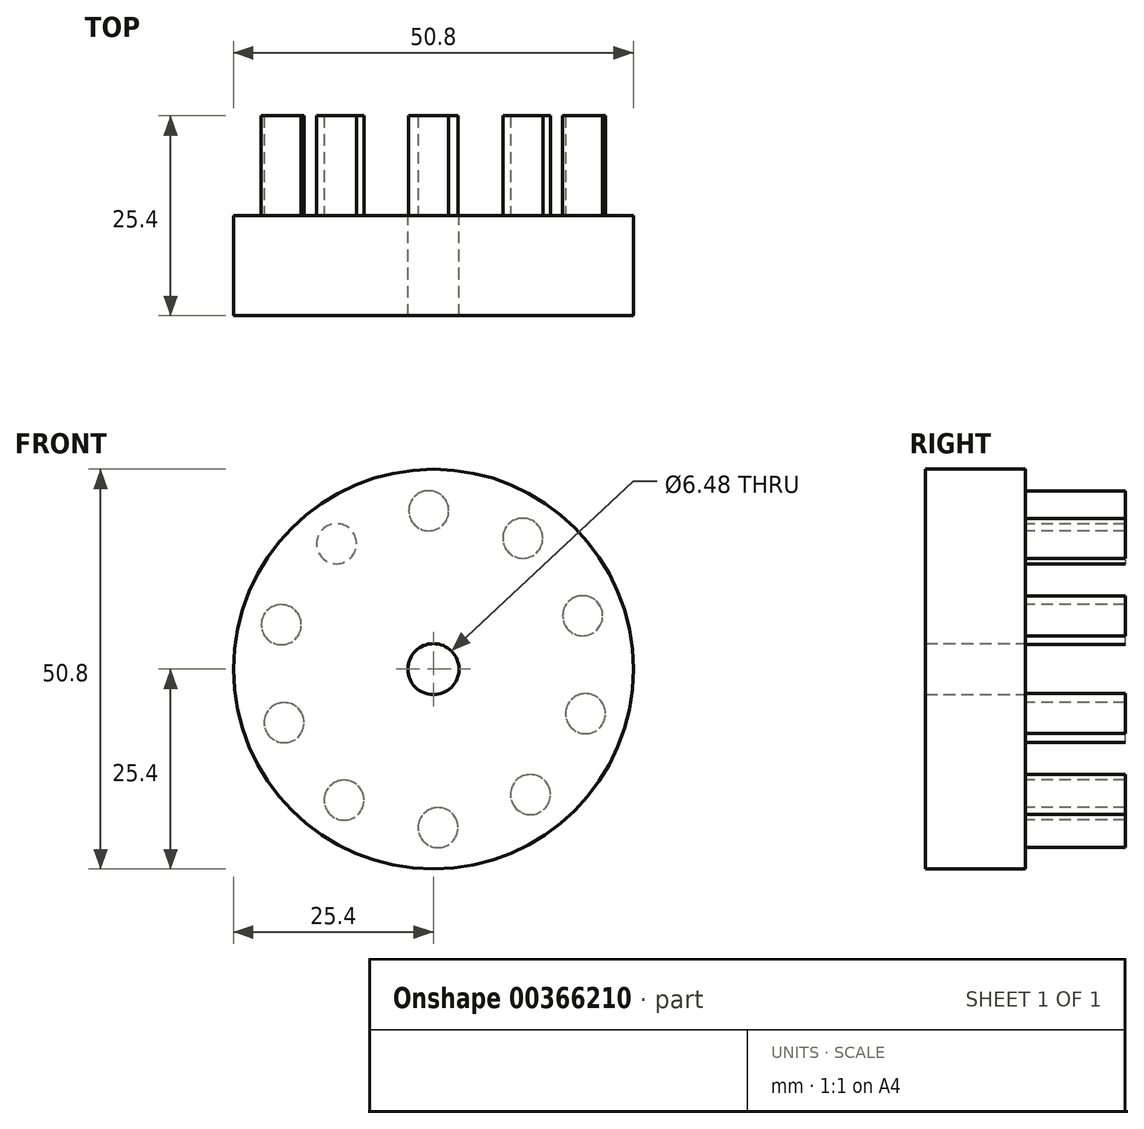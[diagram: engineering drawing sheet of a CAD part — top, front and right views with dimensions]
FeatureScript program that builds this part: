
annotation { "Feature Type Name" : "Feature", "Feature Type Description" : "" }
export const myFeature = defineFeature(function(context is Context, id is Id, definition is map)
    precondition{}
    {
        {
            var Q0;
            Q0=qCreatedBy(makeId("Front.planeOp"),FACE);
            var sketch = newSketch(context, id + "F0", { "sketchPlane" : qUnion([Q0])});
            skCircle(sketch, "E0", {"center": v(0, 0) * mm, "radius": 25.4 * mm});
            skSolve(sketch);
        }
        {
            var Q0;
            Q0=makeQuery(id+"F0.imprint","IMPRINT",FACE,{"disambiguationData":[TD([[makeQuery(id+"F0.imprint","IMPRINT",EDGE,{"derivedFrom":sQuery(id+"F0.wireOp",EDGE,"E0")}),1.0]])]});
            extrude(context, id + "F1", {"entities" : qUnion([Q0]), "depth" : 12.7 * mm});
        }
        {
            var Q0;
            Q0=makeQuery(id+"F1.opExtrude","CAP_FACE",FACE,{"disambiguationData":[OSD([sQuery(id+"F0.wireOp",EDGE,"E0")])],"isStart":true});
            var sketch = newSketch(context, id + "F2", { "sketchPlane" : qUnion([Q0])});
            skCircle(sketch, "E1", {"center": v(12.31, 15.93) * mm, "radius": 2.54 * mm});
            skCircle(sketch, "E2.1.0", {"center": v(0.6, 20.13) * mm, "radius": 2.54 * mm});
            skCircle(sketch, "E2.2.0", {"center": v(-11.35, 16.63) * mm, "radius": 2.54 * mm});
            skCircle(sketch, "E2.3.0", {"center": v(-18.96, 6.79) * mm, "radius": 2.54 * mm});
            skCircle(sketch, "E2.4.0", {"center": v(-19.33, -5.65) * mm, "radius": 2.54 * mm});
            skCircle(sketch, "E2.5.0", {"center": v(-12.31, -15.93) * mm, "radius": 2.54 * mm});
            skCircle(sketch, "E2.6.0", {"center": v(-0.6, -20.13) * mm, "radius": 2.54 * mm});
            skCircle(sketch, "E2.7.0", {"center": v(11.35, -16.63) * mm, "radius": 2.54 * mm});
            skCircle(sketch, "E2.8.0", {"center": v(18.96, -6.79) * mm, "radius": 2.54 * mm});
            skCircle(sketch, "E2.9.0", {"center": v(19.33, 5.65) * mm, "radius": 2.54 * mm});
            skPoint(sketch, "E2.center", {"position": v(0, 0) * mm});
            skSolve(sketch);
        }
        {
            var Q0;
            Q0 = qSketchRegion(id + "F2", true);
            extrude(context, id + "F3", {"entities" : qUnion([Q0]), "operationType" : NewBodyOperationType.ADD, "depth" : 12.7 * mm});
        }
        {
            var Q0;
            Q0=makeQuery(id+"F1.opExtrude","CAP_FACE",FACE,{"disambiguationData":[OSD([sQuery(id+"F0.wireOp",EDGE,"E0")])],"isStart":true});
            var sketch = newSketch(context, id + "F4", { "sketchPlane" : qUnion([Q0])});
            skCircle(sketch, "E3", {"center": v(0, 0) * mm, "radius": 3.24 * mm});
            skSolve(sketch);
        }
        {
            var Q0;
            Q0=makeQuery(id+"F4.imprint","IMPRINT",FACE,{"disambiguationData":[TD([[makeQuery(id+"F4.imprint","IMPRINT",EDGE,{"derivedFrom":sQuery(id+"F4.wireOp",EDGE,"E3")}),1.0]])]});
            extrude(context, id + "F5", {"entities" : qUnion([Q0]), "operationType" : NewBodyOperationType.REMOVE, "oppositeDirection" : true, "depth" : 12.7 * mm});
        }
    });
